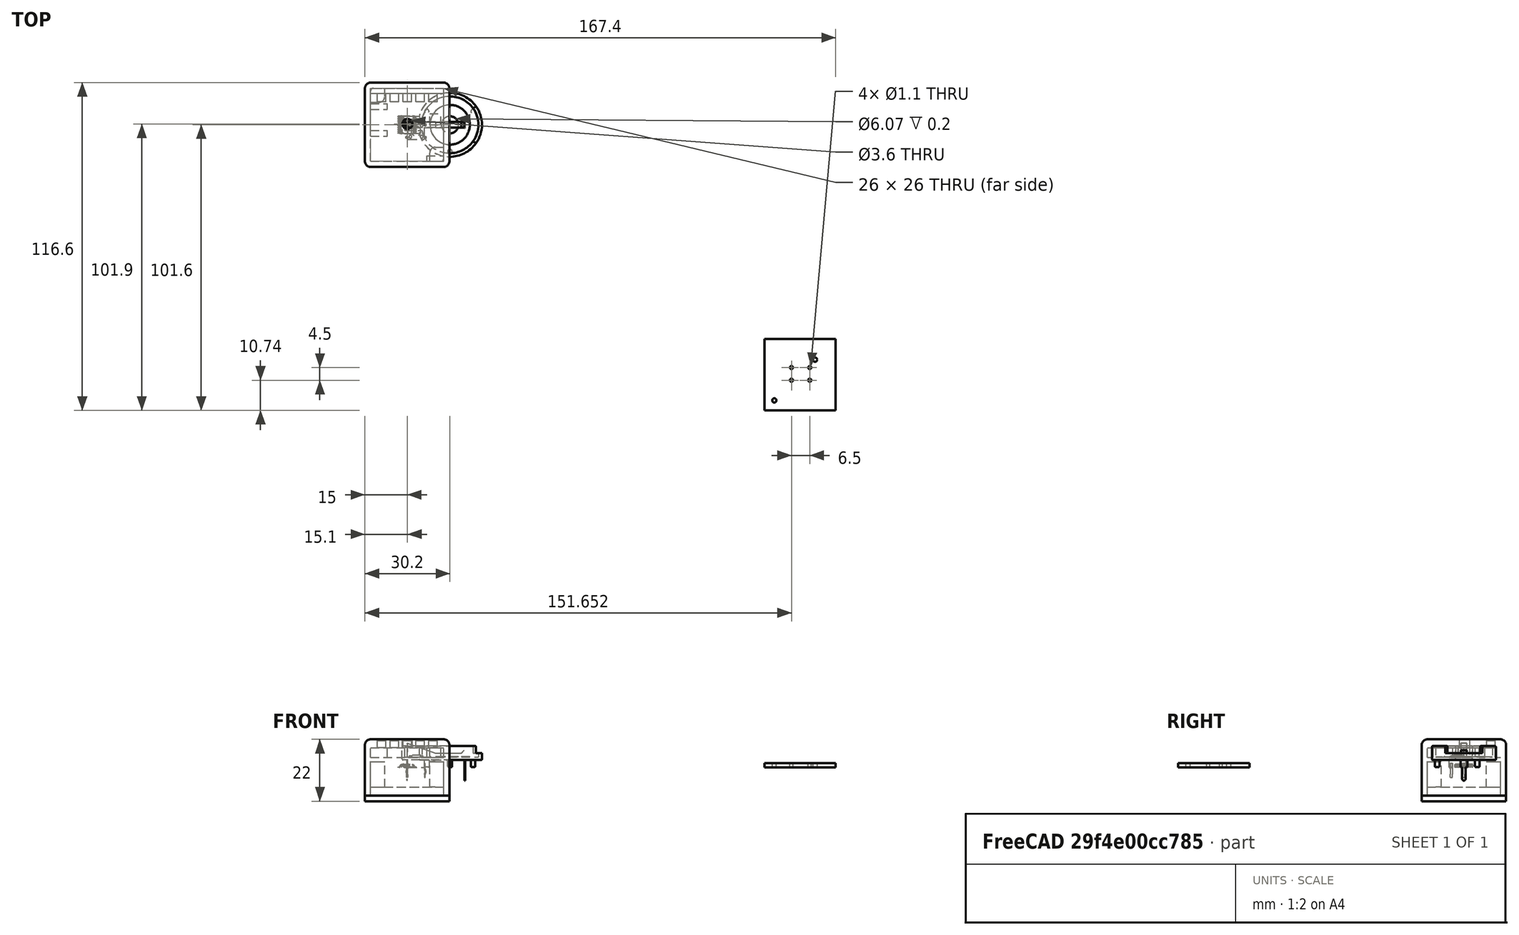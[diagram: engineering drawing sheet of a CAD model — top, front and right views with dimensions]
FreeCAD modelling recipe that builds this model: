
FCSTD DOCUMENT  (FreeCAD 0.17R13541 (Git))
Label: BoxSup
License: All rights reserved
LicenseURL: http://en.wikipedia.org/wiki/All_rights_reserved
objects: Part::Feature×30, App::Part×30, Part::Box×16, Part::MultiFuse×4, Part::Fillet×4, Part::Cut×3, Part::Cylinder×1
note: 58 computed .brp shape members not serialized (recipe doc carries the construction recipe); baked Part::Feature solids carry a one-line shape summary decoded from their .brp

FEATURE [Part::Box] Box  label="MainInside"
  AttacherType = Attacher::AttachEngine3D
  Height = 17
  Length = 26
  Placement = pos=(-13,-13,-10) rot=(0,0,1;0rad)
  Width = 26
FEATURE [Part::Box] Box001  label="MainOutside"
  AttacherType = Attacher::AttachEngine3D
  Height = 20
  Length = 30
  Placement = pos=(-15,-15,-10) rot=(0,0,1;0rad)
  Width = 30
FEATURE [Part::Feature] Part__Feature  label="SOLID"
  shape: bbox 2 x 1.25 x 1.1 mm, 50 faces (baked)
FEATURE [App::Part] LED_0805_2012Metric
  Group = -> [Part__Feature]
  License = CC BY 3.0
  LicenseURL = http://creativecommons.org/licenses/by/3.0/
  Origin = -> Origin
  Placement = pos=(144.272,-79.248,1.65) rot=(0,0,-1;1.5708rad)
FEATURE [Part::Feature] Part__Feature001  label="SOLID001"
  shape: bbox 7.174 x 6 x 7.8 mm, 105 faces (baked)
FEATURE [App::Part] SW_PUSH_6mm
  Group = -> [Part__Feature001]
  License = CC BY 3.0
  LicenseURL = http://creativecommons.org/licenses/by/3.0/
  Origin = -> Origin001
  Placement = pos=(136.652,-86.36,1.65) rot=(0,0,1;0rad)
FEATURE [Part::Feature] Part__Feature002  label="SOLID002"
  shape: bbox 1.6 x 0.8 x 0.45 mm, 26 faces (baked)
FEATURE [App::Part] R_0603_1608Metric
  Group = -> [Part__Feature002]
  License = CC BY 3.0
  LicenseURL = http://creativecommons.org/licenses/by/3.0/
  Origin = -> Origin002
  Placement = pos=(147.701,-98.679,1.65) rot=(0,0,1;0rad)
FEATURE [Part::Feature] Part__Feature003  label="SOLID003"
  shape: bbox 1.6 x 0.8 x 0.45 mm, 26 faces (baked)
FEATURE [App::Part] R_0603_1608Metric001
  Group = -> [Part__Feature003]
  License = CC BY 3.0
  LicenseURL = http://creativecommons.org/licenses/by/3.0/
  Origin = -> Origin003
  Placement = pos=(145.411,-99.187,1.65) rot=(0,0,1;1.5708rad)
FEATURE [Part::Feature] Part__Feature004  label="SOLID004"
  shape: bbox 6.4 x 6.5 x 1.2 mm, 336 faces (baked)
FEATURE [App::Part] TSSOP_20_4_4x6_5mm_P0_65mm
  Group = -> [Part__Feature004]
  License = CC BY 3.0
  LicenseURL = http://creativecommons.org/licenses/by/3.0/
  Origin = -> Origin004
  Placement = pos=(148.336,-93.81,1.65) rot=(0,0,1;1.5708rad)
FEATURE [Part::Feature] Part__Feature005  label="SOLID005"
  shape: bbox 2 x 1.25 x 1.1 mm, 50 faces (baked)
FEATURE [App::Part] LED_0805_2012Metric001
  Group = -> [Part__Feature005]
  License = CC BY 3.0
  LicenseURL = http://creativecommons.org/licenses/by/3.0/
  Origin = -> Origin005
  Placement = pos=(130.556,-79.248,1.65) rot=(0,0,-1;1.5708rad)
FEATURE [Part::Feature] Part__Feature006  label="SOLID006"
  shape: bbox 2 x 1.25 x 1.1 mm, 50 faces (baked)
FEATURE [App::Part] LED_0805_2012Metric002
  Group = -> [Part__Feature006]
  License = CC BY 3.0
  LicenseURL = http://creativecommons.org/licenses/by/3.0/
  Origin = -> Origin006
  Placement = pos=(135.128,-79.248,1.65) rot=(0,0,-1;1.5708rad)
FEATURE [Part::Feature] Part__Feature007  label="SOLID007"
  shape: bbox 2 x 1.25 x 1.1 mm, 50 faces (baked)
FEATURE [App::Part] LED_0805_2012Metric003
  Group = -> [Part__Feature007]
  License = CC BY 3.0
  LicenseURL = http://creativecommons.org/licenses/by/3.0/
  Origin = -> Origin007
  Placement = pos=(139.7,-79.248,1.65) rot=(0,0,-1;1.5708rad)
FEATURE [Part::Feature] Part__Feature008  label="SOLID008"
  shape: bbox 2 x 1.25 x 1.1 mm, 50 faces (baked)
FEATURE [App::Part] LED_0805_2012Metric004
  Group = -> [Part__Feature008]
  License = CC BY 3.0
  LicenseURL = http://creativecommons.org/licenses/by/3.0/
  Origin = -> Origin008
  Placement = pos=(148.844,-79.248,1.65) rot=(0,0,-1;1.5708rad)
FEATURE [Part::Feature] Part__Feature009  label="SOLID009"
  shape: bbox 1.6 x 0.8 x 0.45 mm, 26 faces (baked)
FEATURE [App::Part] R_0603_1608Metric002
  Group = -> [Part__Feature009]
  License = CC BY 3.0
  LicenseURL = http://creativecommons.org/licenses/by/3.0/
  Origin = -> Origin009
  Placement = pos=(132.588,-79.248,1.65) rot=(0,0,-1;1.5708rad)
FEATURE [Part::Feature] Part__Feature010  label="SOLID010"
  shape: bbox 1.6 x 0.8 x 0.45 mm, 26 faces (baked)
FEATURE [App::Part] R_0603_1608Metric003
  Group = -> [Part__Feature010]
  License = CC BY 3.0
  LicenseURL = http://creativecommons.org/licenses/by/3.0/
  Origin = -> Origin010
  Placement = pos=(137.16,-79.248,1.65) rot=(0,0,-1;1.5708rad)
FEATURE [Part::Feature] Part__Feature011  label="SOLID011"
  shape: bbox 1.6 x 0.8 x 0.45 mm, 26 faces (baked)
FEATURE [App::Part] R_0603_1608Metric004
  Group = -> [Part__Feature011]
  License = CC BY 3.0
  LicenseURL = http://creativecommons.org/licenses/by/3.0/
  Origin = -> Origin011
  Placement = pos=(141.732,-79.248,1.65) rot=(0,0,-1;1.5708rad)
FEATURE [Part::Feature] Part__Feature012  label="SOLID012"
  shape: bbox 1.6 x 0.8 x 0.45 mm, 26 faces (baked)
FEATURE [App::Part] R_0603_1608Metric005
  Group = -> [Part__Feature012]
  License = CC BY 3.0
  LicenseURL = http://creativecommons.org/licenses/by/3.0/
  Origin = -> Origin012
  Placement = pos=(146.304,-79.248,1.65) rot=(0,0,-1;1.5708rad)
FEATURE [Part::Feature] Part__Feature013  label="SOLID013"
  shape: bbox 1.6 x 0.8 x 0.45 mm, 26 faces (baked)
FEATURE [App::Part] R_0603_1608Metric006
  Group = -> [Part__Feature013]
  License = CC BY 3.0
  LicenseURL = http://creativecommons.org/licenses/by/3.0/
  Origin = -> Origin013
  Placement = pos=(150.876,-79.248,1.65) rot=(0,0,-1;1.5708rad)
FEATURE [Part::Feature] Part__Feature014  label="SOLID014"
  shape: bbox 1.6 x 0.8 x 0.8 mm, 28 faces (baked)
FEATURE [App::Part] C_0603_1608Metric
  Group = -> [Part__Feature014]
  License = CC BY 3.0
  LicenseURL = http://creativecommons.org/licenses/by/3.0/
  Origin = -> Origin014
  Placement = pos=(142.494,-94.488,1.65) rot=(0,0,-1;1.5708rad)
FEATURE [Part::Feature] Part__Feature015  label="SOLID015"
  shape: bbox 1.6 x 0.8 x 0.8 mm, 28 faces (baked)
FEATURE [App::Part] C_0603_1608Metric001
  Group = -> [Part__Feature015]
  License = CC BY 3.0
  LicenseURL = http://creativecommons.org/licenses/by/3.0/
  Origin = -> Origin015
  Placement = pos=(143.891,-94.488,1.65) rot=(0,0,-1;1.5708rad)
FEATURE [Part::Feature] Part__Feature016  label="SOLID016"
  shape: bbox 1.6 x 0.8 x 0.8 mm, 28 faces (baked)
FEATURE [App::Part] C_0603_1608Metric002
  Group = -> [Part__Feature016]
  License = CC BY 3.0
  LicenseURL = http://creativecommons.org/licenses/by/3.0/
  Origin = -> Origin016
  Placement = pos=(129.286,-95.631,1.65) rot=(0,0,1;0.785398rad)
FEATURE [Part::Feature] Part__Feature017  label="SOLID017"
  shape: bbox 1.6 x 0.8 x 0.8 mm, 28 faces (baked)
FEATURE [App::Part] C_0603_1608Metric003
  Group = -> [Part__Feature017]
  License = CC BY 3.0
  LicenseURL = http://creativecommons.org/licenses/by/3.0/
  Origin = -> Origin017
  Placement = pos=(128.778,-94.107,1.65) rot=(0,0,1;0.785398rad)
FEATURE [Part::Feature] Part__Feature018  label="SOLID018"
  shape: bbox 29.3 x 24.64 x 13.25 mm, 71 faces (baked)
FEATURE [App::Part] BatteryHolder_Keystone_103_1x20mm
  Group = -> [Part__Feature018]
  License = CC BY 3.0
  LicenseURL = http://creativecommons.org/licenses/by/3.0/
  Origin = -> Origin018
  Placement = pos=(130.556,-98.044,-0.05) rot=(0.92388,0.382683,0;3.14159rad)
FEATURE [Part::Feature] Part__Feature019  label="SOLID019"
  shape: bbox 2.5 x 3 x 1.2 mm, 76 faces (baked)
FEATURE [App::Part] SOT_23
  Group = -> [Part__Feature019]
  License = CC BY 3.0
  LicenseURL = http://creativecommons.org/licenses/by/3.0/
  Origin = -> Origin019
  Placement = pos=(130.81,-88.646,1.65) rot=(0,0,1;0rad)
FEATURE [Part::Feature] Part__Feature020  label="SOLID020"
  shape: bbox 2.5 x 3 x 1.2 mm, 76 faces (baked)
FEATURE [App::Part] SOT_23001
  Group = -> [Part__Feature020]
  License = CC BY 3.0
  LicenseURL = http://creativecommons.org/licenses/by/3.0/
  Origin = -> Origin020
  Placement = pos=(129.286,-85.09,1.65) rot=(0,0,1;3.14159rad)
FEATURE [Part::Feature] Part__Feature021  label="SOLID021"
  shape: bbox 1.6 x 0.8 x 0.45 mm, 26 faces (baked)
FEATURE [App::Part] R_0603_1608Metric007
  Group = -> [Part__Feature021]
  License = CC BY 3.0
  LicenseURL = http://creativecommons.org/licenses/by/3.0/
  Origin = -> Origin021
  Placement = pos=(128.27,-88.8745,1.65) rot=(0,0,1;1.5708rad)
FEATURE [Part::Feature] Part__Feature022  label="SOLID022"
  shape: bbox 1.6 x 0.8 x 0.45 mm, 26 faces (baked)
FEATURE [App::Part] R_0603_1608Metric008
  Group = -> [Part__Feature022]
  License = CC BY 3.0
  LicenseURL = http://creativecommons.org/licenses/by/3.0/
  Origin = -> Origin022
  Placement = pos=(131.699,-85.217,1.65) rot=(0,0,1;1.5708rad)
FEATURE [Part::Feature] Part__Feature023  label="SOLID023"
  shape: bbox 2.5 x 3 x 1.2 mm, 76 faces (baked)
FEATURE [App::Part] SOT_23002
  Group = -> [Part__Feature023]
  License = CC BY 3.0
  LicenseURL = http://creativecommons.org/licenses/by/3.0/
  Origin = -> Origin023
  Placement = pos=(135.89,-97.79,1.65) rot=(0,0,1;1.5708rad)
FEATURE [Part::Feature] Part__Feature024  label="SOLID024"
  shape: bbox 2.5 x 3 x 1.2 mm, 76 faces (baked)
FEATURE [App::Part] SOT_23003
  Group = -> [Part__Feature024]
  License = CC BY 3.0
  LicenseURL = http://creativecommons.org/licenses/by/3.0/
  Origin = -> Origin024
  Placement = pos=(139.446,-97.79,1.65) rot=(0,0,1;1.5708rad)
FEATURE [Part::Feature] Part__Feature025  label="SOLID025"
  shape: bbox 2.5 x 3 x 1.2 mm, 76 faces (baked)
FEATURE [App::Part] SOT_23004
  Group = -> [Part__Feature025]
  License = CC BY 3.0
  LicenseURL = http://creativecommons.org/licenses/by/3.0/
  Origin = -> Origin025
  Placement = pos=(143.002,-97.79,1.65) rot=(0,0,1;0rad)
FEATURE [Part::Feature] Part__Feature026  label="SOLID026"
  shape: bbox 1.6 x 0.8 x 0.45 mm, 26 faces (baked)
FEATURE [App::Part] R_0603_1608Metric009
  Group = -> [Part__Feature026]
  License = CC BY 3.0
  LicenseURL = http://creativecommons.org/licenses/by/3.0/
  Origin = -> Origin026
  Placement = pos=(135.89,-100.33,1.65) rot=(0,0,1;3.14159rad)
FEATURE [Part::Feature] Part__Feature027  label="SOLID027"
  shape: bbox 1.6 x 0.8 x 0.45 mm, 26 faces (baked)
FEATURE [App::Part] R_0603_1608Metric010
  Group = -> [Part__Feature027]
  License = CC BY 3.0
  LicenseURL = http://creativecommons.org/licenses/by/3.0/
  Origin = -> Origin027
  Placement = pos=(133.35,-99.5425,1.65) rot=(0,0,-1;1.5708rad)
FEATURE [Part::Feature] Part__Feature028  label="SOLID028"
  shape: bbox 1.6 x 0.8 x 0.45 mm, 26 faces (baked)
FEATURE [App::Part] R_0603_1608Metric011
  Group = -> [Part__Feature028]
  License = CC BY 3.0
  LicenseURL = http://creativecommons.org/licenses/by/3.0/
  Origin = -> Origin028
  Placement = pos=(139.192,-100.33,1.65) rot=(0,0,1;0rad)
FEATURE [Part::Feature] Part__Feature029  label="COMPOUND"
  shape: bbox 25.4 x 25.4 x 1.6 mm, 12 faces (baked)
FEATURE [App::Part] Open_CASCADE_STEP_translator_6_9_1
  Group = -> [LED_0805_2012Metric,SW_PUSH_6mm,R_0603_1608Metric,R_0603_1608Metric001,TSSOP_20_4_4x6_5mm_P0_65mm,LED_0805_2012Metric001,LED_0805_2012Metric002,LED_0805_2012Metric003,LED_0805_2012Metric004,R_0603_1608Metric002,R_0603_1608Metric003,R_0603_1608Metric004,R_0603_1608Metric005,R_0603_1608Metric006,C_0603_1608Metric,C_0603_1608Metric001,C_0603_1608Metric002,C_0603_1608Metric003,+12 more]
  License = CC BY 3.0
  LicenseURL = http://creativecommons.org/licenses/by/3.0/
  Origin = -> Origin029
  Placement = pos=(-139.7,88.9,2) rot=(0,0,1;0rad)
FEATURE [Part::Cut] Cut
  Base = -> Box001
  Tool = -> Box
FEATURE [Part::Box] Box002  label="L1"
  AttacherType = Attacher::AttachEngine3D
  Height = 3
  Length = 3
  Placement = pos=(-10.61,8.11,6.5) rot=(0,0,1;0rad)
  Width = 3
FEATURE [Part::Box] Box003  label="L2"
  AttacherType = Attacher::AttachEngine3D
  Height = 3
  Length = 3
  Placement = pos=(-6.04,8.11,6.5) rot=(0,0,1;0rad)
  Width = 3
FEATURE [Part::Box] Box004  label="L3"
  AttacherType = Attacher::AttachEngine3D
  Height = 3
  Length = 3
  Placement = pos=(-1.47,8.11,6.5) rot=(0,0,1;0rad)
  Width = 3
FEATURE [Part::Box] Box005  label="L4"
  AttacherType = Attacher::AttachEngine3D
  Height = 3
  Length = 3
  Placement = pos=(3.1,8.11,6.5) rot=(0,0,1;0rad)
  Width = 3
FEATURE [Part::Box] Box006  label="L5"
  AttacherType = Attacher::AttachEngine3D
  Height = 3
  Length = 3
  Placement = pos=(7.67,8.11,6.5) rot=(0,0,1;0rad)
  Width = 3
FEATURE [Part::Cylinder] Cylinder001  label="ButTouch"
  Angle = 360
  AttacherType = Attacher::AttachEngine3D
  Height = 3
  Placement = pos=(0.1,0.3,7) rot=(0,0,1;0rad)
  Radius = 1.8
FEATURE [Part::MultiFuse] Fusion
  Shapes = -> [Box002,Box006,Box005,Box003,Box004]
FEATURE [Part::Box] Box007  label="CubeDestek"
  AttacherType = Attacher::AttachEngine3D
  Height = 3.4
  Length = 26
  Placement = pos=(-13,11.2,3.6) rot=(0,0,1;0rad)
  Width = 1.8
FEATURE [Part::Box] Box008  label="CubeDestek2"
  AttacherType = Attacher::AttachEngine3D
  Height = 3.4
  Length = 4
  Placement = pos=(8,0,3.6) rot=(0,0,1;0rad)
  Width = 4
FEATURE [Part::Box] Box009  label="CubeDestek3"
  AttacherType = Attacher::AttachEngine3D
  Height = 3.4
  Length = 6
  Placement = pos=(-13,-4,3.6) rot=(0,0,1;0rad)
  Width = 2
FEATURE [Part::Box] Box010  label="CubeDestek4"
  AttacherType = Attacher::AttachEngine3D
  Height = 3.4
  Length = 6
  Placement = pos=(-13,5.5,3.6) rot=(0,0,1;0rad)
  Width = 2
FEATURE [Part::Box] Box011  label="CubeDestek5"
  AttacherType = Attacher::AttachEngine3D
  Height = 3.4
  Length = 6
  Placement = pos=(7,-13,3.6) rot=(0,0,1;0rad)
  Width = 2
FEATURE [Part::MultiFuse] Fusion002  label="FusionDestek"
  Shapes = -> [Box011,Box010,Box008,Box007,Box009]
FEATURE [Part::Box] Box012  label="KapakGenis"
  AttacherType = Attacher::AttachEngine3D
  Height = 2
  Length = 30
  Placement = pos=(-15,-15,-12) rot=(0,0,1;0rad)
  Width = 30
FEATURE [Part::Box] Box013  label="KapakIc"
  AttacherType = Attacher::AttachEngine3D
  Height = 3
  Length = 26
  Placement = pos=(-13,-13,-10) rot=(0,0,1;0rad)
  Width = 26
FEATURE [Part::Box] Box014  label="KapakCikinti1"
  AttacherType = Attacher::AttachEngine3D
  Height = 9
  Length = 5
  Placement = pos=(-13,8,-7) rot=(0,0,1;0rad)
  Width = 5
FEATURE [Part::Box] Box015  label="KapakCikinti2"
  AttacherType = Attacher::AttachEngine3D
  Height = 9
  Length = 5
  Placement = pos=(8,-13,-7) rot=(0,0,1;0rad)
  Width = 5
FEATURE [Part::MultiFuse] Fusion004  label="kapak"
  Shapes = -> [Box015,Box013,Box014,Box012]
FEATURE [Part::Fillet] Fillet001
  Base = -> Fusion004
  Edges = 4 edges r=2: [Edge41,Edge42,Edge45,Edge47]
FEATURE [Part::Fillet] Fillet002
  Base = -> Fillet001
  Edges = 2 edges r=2: [Edge55,Edge58]
FEATURE [Part::Cut] Cut001
  Base = -> Cut
  Tool = -> Fusion
FEATURE [Part::Cut] Cut002
  Base = -> Cut001
  Tool = -> Cylinder001
FEATURE [Part::MultiFuse] Fusion005
  Shapes = -> [Fusion002,Cut002]
FEATURE [Part::Fillet] Fillet
  Base = -> Fusion005
  Edges = 8 edges r=2: [Edge131,Edge132,Edge133,Edge134,Edge135,Edge136,Edge137,Edge138]
FEATURE [Part::Fillet] Fillet003
  Base = -> Fillet002
  Edges = 2 edges r=1: [Edge38,Edge48]
